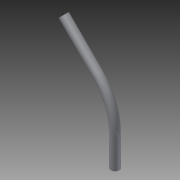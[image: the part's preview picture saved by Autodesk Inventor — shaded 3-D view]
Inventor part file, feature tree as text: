
AUTODESK INVENTOR PART (.ipt)
format: ipt  version: 2014 SP1 (Build 180222100, 222)  size: 116,736 bytes
history: native  units: in
note: dims shown in document units (in); Inventor stores cm internally (conversion verified against a paired STEP export)
features: reference x5, sketch x2, plane x2, sweep x1
ambient origin geometry x8: Origin, YZ Plane, XZ Plane, XY Plane, X Axis, Y Axis, Z Axis, Center Point
bodies: Solid1 (feature_tree)
feature tree (10):
  sketch  "Sketch1"  dims[d0=0.7274in d1=0.7274in]
  plane  "Work Plane2"
  sweep  "Sweep1"
  reference  "Reference1"
  reference  "Reference2"
  reference  "Reference3"
  reference  "Reference4"
  plane  "Work Plane1"
  sketch  "Sketch2"  dims[d2=0.5in d3=0.0in d4=0.45in]
  reference  "Reference5"
